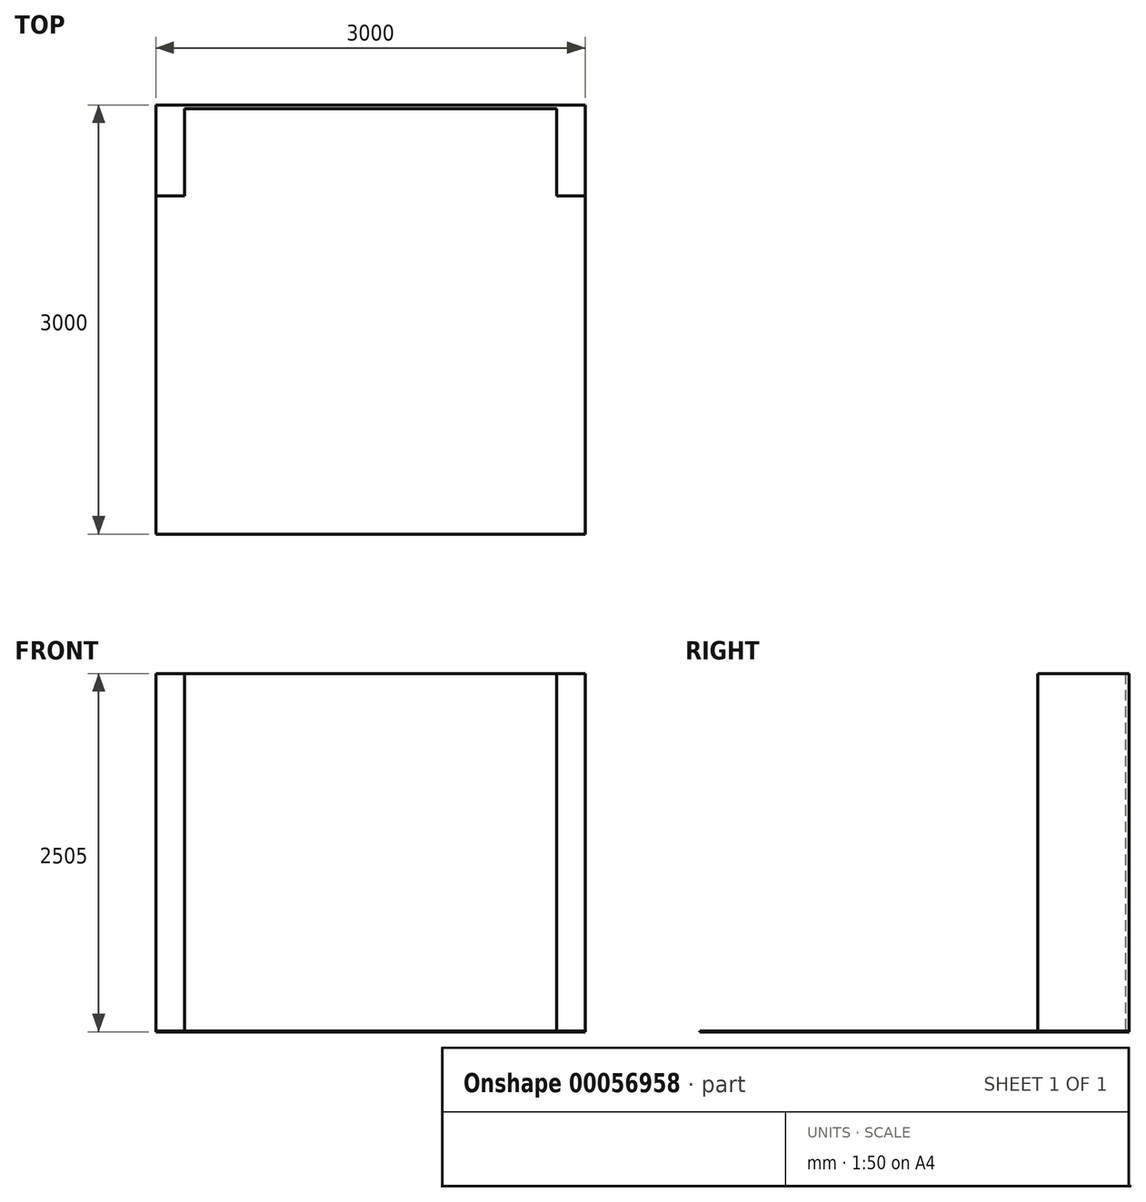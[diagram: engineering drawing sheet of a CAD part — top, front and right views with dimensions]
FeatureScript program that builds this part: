
annotation { "Feature Type Name" : "Feature", "Feature Type Description" : "" }
export const myFeature = defineFeature(function(context is Context, id is Id, definition is map)
    precondition{}
    {
        {
            var Q0;
            Q0=qCreatedBy(makeId("Top.planeOp"),FACE);
            var sketch = newSketch(context, id + "F0", { "sketchPlane" : qUnion([Q0])});
            skLineSegment(sketch, "E0.bottom", {"start": v(0, 0) * mm, "end": v(-3000, 0) * mm});
            skLineSegment(sketch, "E0.top", {"start": v(0, -3000) * mm, "end": v(-3000, -3000) * mm});
            skLineSegment(sketch, "E0.left", {"start": v(0, 0) * mm, "end": v(0, -3000) * mm});
            skLineSegment(sketch, "E0.right", {"start": v(-3000, 0) * mm, "end": v(-3000, -3000) * mm});
            skLineSegment(sketch, "E1", {"start": v(-3000, -637.04) * mm, "end": v(-2800, -637.04) * mm});
            skLineSegment(sketch, "E2", {"start": v(-2800, -637.04) * mm, "end": v(-2800, -25) * mm});
            skLineSegment(sketch, "E3", {"start": v(-2800, -25) * mm, "end": v(-200, -25) * mm});
            skLineSegment(sketch, "E4", {"start": v(-200, -25) * mm, "end": v(-200, -637.04) * mm});
            skLineSegment(sketch, "E5", {"start": v(-200, -637.04) * mm, "end": v(0, -637.04) * mm});
            skSolve(sketch);
        }
        {
            var Q0;
            {var subQ2=sQuery(id+"F0.wireOp",EDGE,"E0.top");Q0=makeQuery(id+"F0.imprint","IMPRINT",FACE,{"disambiguationData":[TD([[makeQuery(id+"F0.imprint","IMPRINT",EDGE,{"derivedFrom":subQ2}),-1.0]])]});}
            var Q1;
            {var subQ2=sQuery(id+"F0.wireOp",EDGE,"E0.bottom");Q1=makeQuery(id+"F0.imprint","IMPRINT",FACE,{"disambiguationData":[TD([[makeQuery(id+"F0.imprint","IMPRINT",EDGE,{"derivedFrom":subQ2}),1.0]])]});}
            extrude(context, id + "F1", {"entities" : qUnion([Q0, Q1]), "oppositeDirection" : true, "depth" : 5 * mm});
        }
        {
            var Q0;
            {var subQ2=sQuery(id+"F0.wireOp",EDGE,"E0.bottom");Q0=makeQuery(id+"F0.imprint","IMPRINT",FACE,{"disambiguationData":[TD([[makeQuery(id+"F0.imprint","IMPRINT",EDGE,{"derivedFrom":subQ2}),1.0]])]});}
            extrude(context, id + "F2", {"entities" : qUnion([Q0]), "depth" : 2500 * mm});
        }
    });
